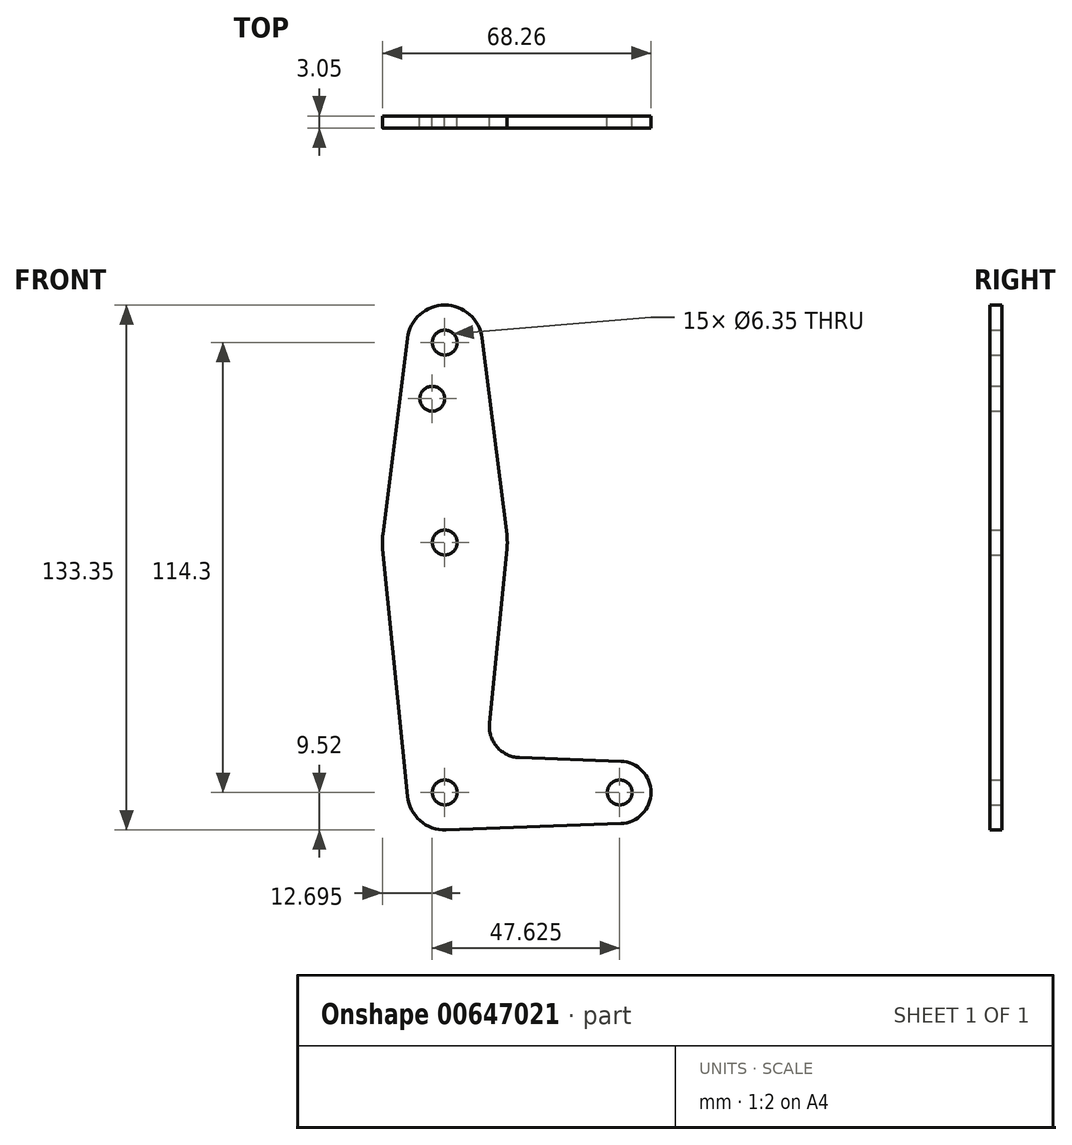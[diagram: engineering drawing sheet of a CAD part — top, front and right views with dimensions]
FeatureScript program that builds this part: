
annotation { "Feature Type Name" : "Feature", "Feature Type Description" : "" }
export const myFeature = defineFeature(function(context is Context, id is Id, definition is map)
    precondition{}
    {
        {
            var Q0;
            Q0=qCreatedBy(makeId("Front.planeOp"),FACE);
            var sketch = newSketch(context, id + "F0", { "sketchPlane" : qUnion([Q0])});
            skLineSegment(sketch, "E0", {"start": v(0, 114.3) * mm, "end": v(0, 0) * mm, "construction": true});
            skLineSegment(sketch, "E1", {"start": v(0, 0) * mm, "end": v(44.45, 0) * mm, "construction": true});
            skCircle(sketch, "E2", {"center": v(0, 114.3) * mm, "radius": 9.53 * mm});
            skCircle(sketch, "E3", {"center": v(0, 0) * mm, "radius": 9.53 * mm});
            skCircle(sketch, "E4", {"center": v(0, 63.5) * mm, "radius": 15.88 * mm});
            skCircle(sketch, "E5", {"center": v(44.45, 0) * mm, "radius": 7.94 * mm});
            skLineSegment(sketch, "E6", {"start": v(9.45, 115.5) * mm, "end": v(15.75, 65.48) * mm});
            skLineSegment(sketch, "E7", {"start": v(-15.75, 65.48) * mm, "end": v(-9.45, 115.5) * mm});
            skLineSegment(sketch, "E8", {"start": v(-15.8, 61.91) * mm, "end": v(-9.48, -0.95) * mm});
            skLineSegment(sketch, "E9", {"start": v(11.34, 17.6) * mm, "end": v(15.8, 61.91) * mm});
            skLineSegment(sketch, "E10", {"start": v(44.73, 7.93) * mm, "end": v(18.97, 8.85) * mm});
            skLineSegment(sketch, "E11", {"start": v(0, -9.53) * mm, "end": v(44.73, -7.93) * mm});
            skCircle(sketch, "E12", {"center": v(0, 114.3) * mm, "radius": 3.18 * mm});
            skCircle(sketch, "E13", {"center": v(0, 63.5) * mm, "radius": 3.18 * mm});
            skCircle(sketch, "E14", {"center": v(0, 0) * mm, "radius": 3.18 * mm});
            skCircle(sketch, "E15", {"center": v(44.45, 0) * mm, "radius": 3.18 * mm});
            skCircle(sketch, "E16", {"center": v(-3.17, 100.03) * mm, "radius": 3.18 * mm});
            skArc(sketch, "E17.filletArc", {"start": v(11.34, 17.6) * mm, "mid": v(13.26, 11.57) * mm, "end": v(18.97, 8.85) * mm});
            skSolve(sketch);
        }
        {
            var Q0;
            Q0 = qSketchRegion(id + "F0", true);
            extrude(context, id + "F1", {"entities" : qUnion([Q0]), "depth" : 3.05 * mm, "offsetDistance" : 25.4 * mm});
        }
    });
